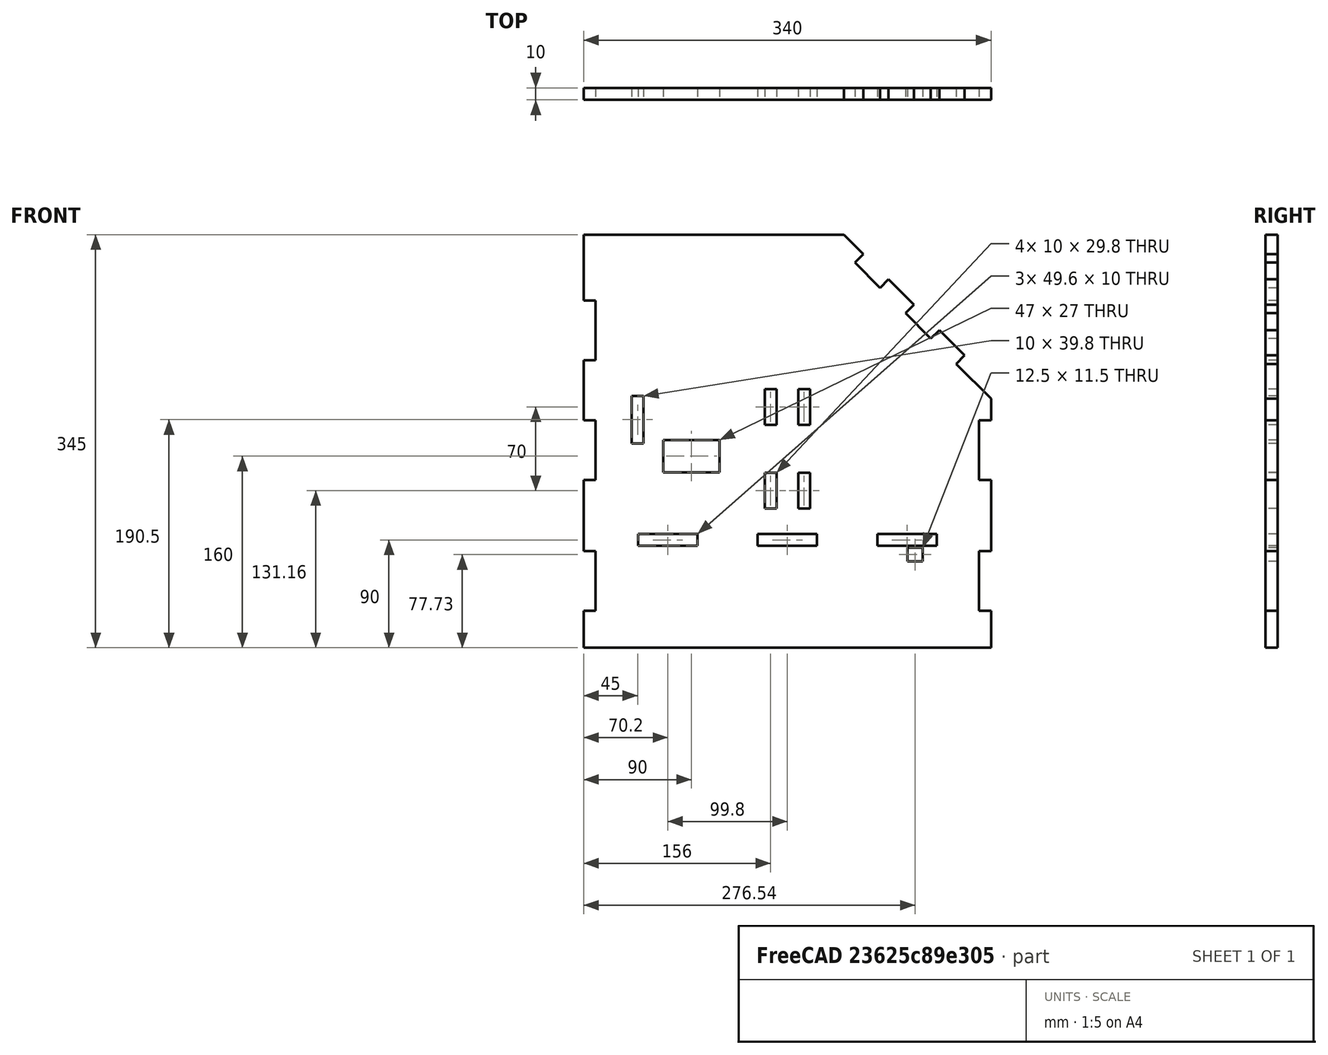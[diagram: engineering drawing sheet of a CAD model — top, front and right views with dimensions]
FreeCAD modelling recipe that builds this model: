
FCSTD DOCUMENT  (FreeCAD 0.19R19327 (Git))
Label: Lateral_derecho
License: All rights reserved
LicenseURL: http://en.wikipedia.org/wiki/All_rights_reserved
objects: Sketcher::SketchObject×1, PartDesign::Pad×1, PartDesign::Body×1
note: 4 computed .brp shape members not serialized (recipe doc carries the construction recipe); baked Part::Feature solids carry a one-line shape summary decoded from their .brp

FEATURE [Sketcher::SketchObject] Sketch
  MapMode = 5
  Placement = pos=(0,0,0) rot=(1,0,0;1.5708rad)
  Support = -> [XZ_Plane]
  sketch-geometry (84):
    g0: LineSegment StartX=0 StartY=0 StartZ=0 EndX=0 EndY=30.933 EndZ=0
    g1: LineSegment StartX=0 StartY=30.933 StartZ=0 EndX=10 EndY=30.933 EndZ=0
    g2: LineSegment StartX=10 StartY=30.933 StartZ=0 EndX=10 EndY=80.733 EndZ=0
    g3: LineSegment StartX=10 StartY=80.733 StartZ=0 EndX=0 EndY=80.733 EndZ=0
    g4: LineSegment StartX=0 StartY=80.733 StartZ=0 EndX=0 EndY=140.2 EndZ=0
    g5: LineSegment StartX=0 StartY=140.2 StartZ=0 EndX=10 EndY=140.2 EndZ=0
    g6: LineSegment StartX=10 StartY=140.2 StartZ=0 EndX=10 EndY=190 EndZ=0
    g7: LineSegment StartX=10 StartY=190 StartZ=0 EndX=0 EndY=190 EndZ=0
    g8: LineSegment StartX=0 StartY=190 StartZ=0 EndX=0 EndY=240 EndZ=0
    g9: LineSegment StartX=0 StartY=240 StartZ=0 EndX=10 EndY=240 EndZ=0
    g10: LineSegment StartX=10 StartY=240 StartZ=0 EndX=10 EndY=289.8 EndZ=0
    g11: LineSegment StartX=10 StartY=289.8 StartZ=0 EndX=0 EndY=289.8 EndZ=0
    g12: LineSegment StartX=0 StartY=289.8 StartZ=0 EndX=0 EndY=345 EndZ=0
    g13: LineSegment StartX=0 StartY=345 StartZ=0 EndX=217.071 EndY=345 EndZ=0
    g14: LineSegment StartX=217.071 StartY=345 StartZ=0 EndX=233.405 EndY=328.666 EndZ=0
    g15: LineSegment StartX=233.405 StartY=328.666 StartZ=0 EndX=226.334 EndY=321.595 EndZ=0
    g16: LineSegment StartX=226.334 StartY=321.595 StartZ=0 EndX=247.406 EndY=300.523 EndZ=0
    g17: LineSegment StartX=247.406 StartY=300.523 StartZ=0 EndX=254.477 EndY=307.594 EndZ=0
    g18: LineSegment StartX=254.477 StartY=307.594 StartZ=0 EndX=275.69 EndY=286.381 EndZ=0
    g19: LineSegment StartX=275.69 StartY=286.381 StartZ=0 EndX=268.619 EndY=279.31 EndZ=0
    g20: LineSegment StartX=268.619 StartY=279.31 StartZ=0 EndX=289.691 EndY=258.238 EndZ=0
    g21: LineSegment StartX=289.691 StartY=258.238 StartZ=0 EndX=296.762 EndY=265.309 EndZ=0
    g22: LineSegment StartX=296.762 StartY=265.309 StartZ=0 EndX=317.975 EndY=244.096 EndZ=0
    g23: LineSegment StartX=317.975 StartY=244.096 StartZ=0 EndX=310.904 EndY=237.025 EndZ=0
    g24: LineSegment StartX=310.904 StartY=237.025 StartZ=0 EndX=340 EndY=207.929 EndZ=0
    g25: LineSegment StartX=340 StartY=207.929 StartZ=0 EndX=340 EndY=190 EndZ=0
    g26: LineSegment StartX=340 StartY=190 StartZ=0 EndX=330 EndY=190 EndZ=0
    g27: LineSegment StartX=330 StartY=190 StartZ=0 EndX=330 EndY=140.2 EndZ=0
    g28: LineSegment StartX=330 StartY=140.2 StartZ=0 EndX=340 EndY=140.2 EndZ=0
    g29: LineSegment StartX=340 StartY=140.2 StartZ=0 EndX=340 EndY=80.733 EndZ=0
    g30: LineSegment StartX=340 StartY=80.733 StartZ=0 EndX=330 EndY=80.733 EndZ=0
    g31: LineSegment StartX=330 StartY=80.733 StartZ=0 EndX=330 EndY=30.933 EndZ=0
    g32: LineSegment StartX=330 StartY=30.933 StartZ=0 EndX=340 EndY=30.933 EndZ=0
    g33: LineSegment StartX=340 StartY=30.933 StartZ=0 EndX=340 EndY=0 EndZ=0
    g34: LineSegment StartX=340 StartY=0 StartZ=0 EndX=0 EndY=0 EndZ=0
    g35: LineSegment [constr] StartX=4e-16 StartY=85 StartZ=0 EndX=340 EndY=85 EndZ=0
    g36: LineSegment StartX=45.4 StartY=85 StartZ=0 EndX=95 EndY=85 EndZ=0
    g37: LineSegment StartX=95 StartY=85 StartZ=0 EndX=95 EndY=95 EndZ=0
    g38: LineSegment StartX=95 StartY=95 StartZ=0 EndX=45.4 EndY=95 EndZ=0
    g39: LineSegment StartX=45.4 StartY=95 StartZ=0 EndX=45.4 EndY=85 EndZ=0
    g40: LineSegment StartX=145.2 StartY=85 StartZ=0 EndX=194.8 EndY=85 EndZ=0
    g41: LineSegment StartX=194.8 StartY=85 StartZ=0 EndX=194.8 EndY=95 EndZ=0
    g42: LineSegment StartX=194.8 StartY=95 StartZ=0 EndX=145.2 EndY=95 EndZ=0
    g43: LineSegment StartX=145.2 StartY=95 StartZ=0 EndX=145.2 EndY=85 EndZ=0
    g44: LineSegment StartX=245 StartY=85 StartZ=0 EndX=294.6 EndY=85 EndZ=0
    g45: LineSegment StartX=294.6 StartY=85 StartZ=0 EndX=294.6 EndY=95 EndZ=0
    g46: LineSegment StartX=294.6 StartY=95 StartZ=0 EndX=245 EndY=95 EndZ=0
    g47: LineSegment StartX=245 StartY=95 StartZ=0 EndX=245 EndY=85 EndZ=0
    g48: LineSegment [constr] StartX=95 StartY=95 StartZ=0 EndX=145.2 EndY=95 EndZ=0
    g49: LineSegment [constr] StartX=194.8 StartY=95 StartZ=0 EndX=245 EndY=95 EndZ=0
    g50: LineSegment [constr] StartX=45.4 StartY=95 StartZ=0 EndX=0 EndY=95 EndZ=0
    g51: LineSegment [constr] StartX=294.6 StartY=95 StartZ=0 EndX=340 EndY=95 EndZ=0
    g52: LineSegment StartX=40 StartY=210.4 StartZ=0 EndX=50 EndY=210.4 EndZ=0
    g53: LineSegment StartX=50 StartY=210.4 StartZ=0 EndX=50 EndY=170.6 EndZ=0
    g54: LineSegment StartX=50 StartY=170.6 StartZ=0 EndX=40 EndY=170.6 EndZ=0
    g55: LineSegment StartX=40 StartY=170.6 StartZ=0 EndX=40 EndY=210.4 EndZ=0
    g56: LineSegment StartX=66.5 StartY=173.5 StartZ=0 EndX=113.5 EndY=173.5 EndZ=0
    g57: LineSegment StartX=113.5 StartY=173.5 StartZ=0 EndX=113.5 EndY=146.5 EndZ=0
    g58: LineSegment StartX=113.5 StartY=146.5 StartZ=0 EndX=66.5 EndY=146.5 EndZ=0
    g59: LineSegment StartX=66.5 StartY=146.5 StartZ=0 EndX=66.5 EndY=173.5 EndZ=0
    g60: LineSegment StartX=151 StartY=216.06 StartZ=0 EndX=161 EndY=216.06 EndZ=0
    g61: LineSegment StartX=161 StartY=216.06 StartZ=0 EndX=161 EndY=186.26 EndZ=0
    g62: LineSegment StartX=161 StartY=186.26 StartZ=0 EndX=151 EndY=186.26 EndZ=0
    g63: LineSegment StartX=151 StartY=186.26 StartZ=0 EndX=151 EndY=216.06 EndZ=0
    g64: LineSegment StartX=179 StartY=216.06 StartZ=0 EndX=189 EndY=216.06 EndZ=0
    g65: LineSegment StartX=189 StartY=216.06 StartZ=0 EndX=189 EndY=186.26 EndZ=0
    g66: LineSegment StartX=189 StartY=186.26 StartZ=0 EndX=179 EndY=186.26 EndZ=0
    g67: LineSegment StartX=179 StartY=186.26 StartZ=0 EndX=179 EndY=216.06 EndZ=0
    g68: LineSegment StartX=151 StartY=146.06 StartZ=0 EndX=161 EndY=146.06 EndZ=0
    g69: LineSegment StartX=161 StartY=146.06 StartZ=0 EndX=161 EndY=116.26 EndZ=0
    g70: LineSegment StartX=161 StartY=116.26 StartZ=0 EndX=151 EndY=116.26 EndZ=0
    g71: LineSegment StartX=151 StartY=116.26 StartZ=0 EndX=151 EndY=146.06 EndZ=0
    g72: LineSegment StartX=179 StartY=146.06 StartZ=0 EndX=189 EndY=146.06 EndZ=0
    g73: LineSegment StartX=189 StartY=146.06 StartZ=0 EndX=189 EndY=116.26 EndZ=0
    g74: LineSegment StartX=189 StartY=116.26 StartZ=0 EndX=179 EndY=116.26 EndZ=0
    g75: LineSegment StartX=179 StartY=116.26 StartZ=0 EndX=179 EndY=146.06 EndZ=0
    g76: LineSegment StartX=270.29 StartY=83.48 StartZ=0 EndX=282.79 EndY=83.48 EndZ=0
    g77: LineSegment StartX=282.79 StartY=83.48 StartZ=0 EndX=282.79 EndY=71.98 EndZ=0
    g78: LineSegment StartX=282.79 StartY=71.98 StartZ=0 EndX=270.29 EndY=71.98 EndZ=0
    g79: LineSegment StartX=270.29 StartY=71.98 StartZ=0 EndX=270.29 EndY=83.48 EndZ=0
    g80: LineSegment [constr] StartX=151 StartY=116.26 StartZ=0 EndX=189 EndY=116.26 EndZ=0
    g81: LineSegment [constr] StartX=189 StartY=116.26 StartZ=0 EndX=189 EndY=216.06 EndZ=0
    g82: LineSegment [constr] StartX=189 StartY=216.06 StartZ=0 EndX=151 EndY=216.06 EndZ=0
    g83: LineSegment [constr] StartX=151 StartY=216.06 StartZ=0 EndX=151 EndY=116.26 EndZ=0
  constraints (246):
    c: Coincident(g-1,g0)
    c: PointOnObject(g0,g-2)
    c: Coincident(g0,g1)
    c: Horizontal(g1)
    c: Coincident(g1,g2)
    c: Vertical(g2)
    c: Coincident(g2,g3)
    c: Horizontal(g3)
    c: Coincident(g3,g4)
    c: PointOnObject(g4,g-2)
    c: Coincident(g4,g5)
    c: Horizontal(g5)
    c: Coincident(g5,g6)
    c: Vertical(g6)
    c: Coincident(g6,g7)
    c: Horizontal(g7)
    c: Coincident(g7,g8)
    c: Vertical(g8)
    c: Coincident(g8,g9)
    c: Horizontal(g9)
    c: Coincident(g9,g10)
    c: Vertical(g10)
    c: Coincident(g10,g11)
    c: Horizontal(g11)
    c: Coincident(g11,g12)
    c: PointOnObject(g12,g-2)
    c: Coincident(g12,g13)
    c: Horizontal(g13)
    c: Coincident(g13,g14)
    c: Coincident(g14,g15)
    c: Coincident(g15,g16)
    c: Coincident(g16,g17)
    c: Coincident(g17,g18)
    c: Coincident(g18,g19)
    c: Coincident(g19,g20)
    c: Coincident(g20,g21)
    c: Coincident(g21,g22)
    c: Coincident(g22,g23)
    c: Coincident(g23,g24)
    c: Coincident(g24,g25)
    c: Coincident(g25,g26)
    c: Coincident(g26,g27)
    c: Coincident(g27,g28)
    c: Coincident(g28,g29)
    c: Vertical(g29)
    c: Coincident(g29,g30)
    c: Horizontal(g30)
    c: Coincident(g30,g31)
    c: Vertical(g31)
    c: Coincident(g31,g32)
    c: Horizontal(g32)
    c: Coincident(g32,g33)
    c: PointOnObject(g33,g-1)
    c: Coincident(g33,g34)
    c: Coincident(g34,g0)
    c: Horizontal(g26)
    c: Horizontal(g28)
    c: Vertical(g27)
    c: Vertical(g33)
    c: Equal(g1,g3)
    c: Equal(g3,g5)
    c: Equal(g5,g7)
    c: Equal(g7,g9)
    c: Equal(g9,g11)
    c: Equal(g11,g26)
    c: Equal(g26,g28)
    c: Equal(g28,g30)
    c: Equal(g30,g32)
    c: Equal(g32,g15)
    c: Equal(g15,g17)
    c: Equal(g17,g19)
    c: Equal(g19,g21)
    c: Equal(g21,g23)
    c: DistanceX(g1,g1) = 10
    c: Vertical(g25)
    c: Angle(g13,g14) = 2.35619
    c: Parallel(g16,g14)
    c: Parallel(g18,g16)
    c: Parallel(g20,g18)
    c: Parallel(g22,g20)
    c: Parallel(g24,g22)
    c: Perpendicular(g15,g14)
    c: Perpendicular(g16,g17)
    c: Perpendicular(g18,g19)
    c: Perpendicular(g20,g21)
    c: Perpendicular(g22,g23)
    c: Equal(g16,g20)
    c: Distance(g16) = 29.8
    c: Distance(g14) = 23.1
    c: Equal(g18,g22)
    c: Distance(g18) = 30
    c: Distance(g24) = 41.148
    c: DistanceX(g34,g34) = 340
    c: Equal(g2,g6)
    c: Equal(g6,g10)
    c: DistanceY(g10,g10) = 49.8
    c: DistanceY(g12,g12) = 55.2
    c: DistanceY(g0,g12) = 345
    c: Equal(g6,g27)
    c: Equal(g27,g31)
    c: DistanceY(g25,g25) = 17.929
    c: Equal(g33,g0)
    c: DistanceY(g0,g0) = 30.933
    c: DistanceY(g8,g8) = 50
    c: PointOnObject(g35,g4)
    c: PointOnObject(g35,g29)
    c: Horizontal(g35)
    c: Coincident(g36,g37)
    c: Coincident(g37,g38)
    c: Coincident(g38,g39)
    c: Coincident(g39,g36)
    c: Horizontal(g36)
    c: Horizontal(g38)
    c: Vertical(g37)
    c: Vertical(g39)
    c: PointOnObject(g36,g35)
    c: Coincident(g40,g41)
    c: Coincident(g41,g42)
    c: Coincident(g42,g43)
    c: Coincident(g43,g40)
    c: Horizontal(g40)
    c: Horizontal(g42)
    c: Vertical(g41)
    c: Vertical(g43)
    c: PointOnObject(g40,g35)
    c: Coincident(g44,g45)
    c: Coincident(g45,g46)
    c: Coincident(g46,g47)
    c: Coincident(g47,g44)
    c: Horizontal(g44)
    c: Horizontal(g46)
    c: Vertical(g45)
    c: Vertical(g47)
    c: PointOnObject(g44,g35)
    c: Equal(g39,g43)
    c: Equal(g43,g47)
    c: Equal(g38,g42)
    c: Equal(g42,g46)
    c: Coincident(g48,g37)
    c: Coincident(g48,g42)
    c: Coincident(g49,g41)
    c: Coincident(g49,g46)
    c: Equal(g48,g49)
    c: DistanceX(g38,g38) = 49.6
    c: DistanceY(g39,g39) = 10
    c: DistanceX(g48,g48) = 50.2
    c: Coincident(g50,g38)
    c: PointOnObject(g50,g4)
    c: Horizontal(g50)
    c: Coincident(g51,g45)
    c: PointOnObject(g51,g29)
    c: Horizontal(g51)
    c: Equal(g51,g50)
    c: DistanceY(g0,g35) = 85
    c: Coincident(g52,g53)
    c: Coincident(g53,g54)
    c: Coincident(g54,g55)
    c: Coincident(g55,g52)
    c: Horizontal(g52)
    c: Horizontal(g54)
    c: Vertical(g53)
    c: Vertical(g55)
    c: Coincident(g56,g57)
    c: Coincident(g57,g58)
    c: Coincident(g58,g59)
    c: Coincident(g59,g56)
    c: Horizontal(g56)
    c: Horizontal(g58)
    c: Vertical(g57)
    c: Vertical(g59)
    c: Coincident(g60,g61)
    c: Coincident(g61,g62)
    c: Coincident(g62,g63)
    c: Coincident(g63,g60)
    c: Horizontal(g60)
    c: Horizontal(g62)
    c: Vertical(g61)
    c: Vertical(g63)
    c: Coincident(g64,g65)
    c: Coincident(g65,g66)
    c: Coincident(g66,g67)
    c: Coincident(g67,g64)
    c: Horizontal(g64)
    c: Horizontal(g66)
    c: Vertical(g65)
    c: Vertical(g67)
    c: Coincident(g68,g69)
    c: Coincident(g69,g70)
    c: Coincident(g70,g71)
    c: Coincident(g71,g68)
    c: Horizontal(g68)
    c: Horizontal(g70)
    c: Vertical(g69)
    c: Vertical(g71)
    c: Coincident(g72,g73)
    c: Coincident(g73,g74)
    c: Coincident(g74,g75)
    c: Coincident(g75,g72)
    c: Horizontal(g72)
    c: Horizontal(g74)
    c: Vertical(g73)
    c: Vertical(g75)
    c: Coincident(g76,g77)
    c: Coincident(g77,g78)
    c: Coincident(g78,g79)
    c: Coincident(g79,g76)
    c: Horizontal(g76)
    c: Horizontal(g78)
    c: Vertical(g77)
    c: Vertical(g79)
    c: DistanceX(g56,g56) = 47
    c: DistanceY(g59,g59) = 27
    c: Equal(g52,g60)
    c: Equal(g60,g64)
    c: Equal(g64,g68)
    c: Equal(g68,g72)
    c: Equal(g63,g67)
    c: Equal(g67,g75)
    c: Equal(g75,g71)
    c: DistanceY(g55,g55) = 39.8
    c: DistanceY(g63,g63) = 29.8
    c: Coincident(g80,g81)
    c: Coincident(g81,g82)
    c: Coincident(g82,g83)
    c: Coincident(g83,g80)
    c: Horizontal(g80)
    c: Horizontal(g82)
    c: Vertical(g81)
    c: Vertical(g83)
    c: Coincident(g80,g70)
    c: Coincident(g60,g82)
    c: Coincident(g64,g81)
    c: Coincident(g73,g80)
    c: DistanceY(g83,g83) = 99.8
    c: DistanceX(g82,g82) = 38
    c: DistanceX(g76,g76) = 12.5
    c: DistanceY(g79,g79) = 11.5
    c: DistanceY(g0,g54) = 170.6
    c: DistanceX(g0,g54) = 40
    c: DistanceX(g54,g54) = 10
    c: DistanceY(g0,g58) = 146.5
    c: DistanceX(g0,g58) = 66.5
    c: DistanceX(g0,g70) = 151
    c: DistanceY(g0,g70) = 116.26
    c: DistanceX(g0,g78) = 270.29
    c: DistanceY(g0,g78) = 71.98
FEATURE [PartDesign::Pad] Pad
  Length = 10
  Length2 = 100
  Placement = pos=(0,0,0) rot=(1,0,0;1.5708rad)
  Profile = -> Sketch
  Type = 0
FEATURE [PartDesign::Body] Body
  Group = -> [Sketch,Pad]
  Origin = -> Origin
  Tip = -> Pad
